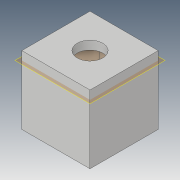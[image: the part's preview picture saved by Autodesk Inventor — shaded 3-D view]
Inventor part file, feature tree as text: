
AUTODESK INVENTOR PART (.ipt)
format: ipt  version: 2019 (Build 230136000, 136)  size: 100,864 bytes
history: native  units: mm
features: extrude x2, sketch x2, plane x1
ambient origin geometry x8: Origin, YZ Plane, XZ Plane, XY Plane, X Axis, Y Axis, Z Axis, Center Point
bodies: Solid1 (feature_tree)
feature tree (5):
  extrude  "Extrusion1"  Depth=6.0mm
  plane  "Work Plane1"
  extrude  "Extrusion2"  Depth=3.15mm
  sketch  "Sketch1"  dims[d0=4.5mm d1=6.0mm]
  sketch  "Sketch2"  dims[d2=6.0mm d3=6.0mm d4=6.0mm d5=12.0mm d6=0.0mm d7=-1.5mm d8=7.5mm d9=3.15mm d10=0.0mm]
